# Revit family: APL Metro Series Thermal Heart Hinged Door Open In
name_source: partatom
category: Doors
revit_build: Autodesk Revit LT 2018 (Build: 20170223_1515(x64)
units: mm (PartAtom-declared; Revit-internal decimal feet)

## family parameters
Always vertical = Yes
Cut with Voids When Loaded = No
Host = Wall
OmniClass Number = 23.30.10.00
OmniClass Title = Doors
Room Calculation Point = No
Shared = No

## types (4) — shared parameters
15° Opening = Yes
90° Opening = No
Analytic Construction = <None>
Frame Projection Ext. = 13 mm
Frame Projection Int. = 20 mm  [stored 0.0656168 ft]
Frame Width = 13 mm
Frame Width Sill = 15 mm  [stored 0.0492126 ft]
Function = Interior
Groove = 10 mm  [stored 0.0328084 ft]
Handle = Yes
Handle External = Yes
Handle Internal = Yes
Jamb Liner 1 = Yes
Jamb Liner 2 = Yes
Liner End = 10 mm  [stored 0.0328084 ft]
Liner Head = Yes
Liner Sill = No
Lock External = Yes
Lock Internal = Yes
Opening = Yes
Rough Width = 815 mm  [stored 2.67388 ft]
Wall Closure = By host
Width = 800 mm  [stored 2.62467 ft]
zero-valued in all types: Thickness

## per-type parameters (varying)
| type | Architrave | DG Liner | DG Liner No Groove | Height | Reveal Liner | Rough Height | SG Liner | SG Liner No Groove |
| Architrave (DG) | Yes | No | Yes | 2201 mm | No | 2213 mm | No | No |
| Architrave (SG) | Yes | No | No | 2203 mm | No | 2215 mm  [stored 7.26706 ft] | No | Yes |
| Liner (DG) | No | Yes | No | 2203 mm | Yes | 2215 mm  [stored 7.26706 ft] | No | No |
| Liner (SG) | No | No | No | 2203 mm | Yes | 2215 mm  [stored 7.26706 ft] | Yes | No |

note: [stored X ft] marks values corroborated as IEEE doubles in the binary element streams (Revit-internal decimal feet)

## geometry (parser evidence)
native form markers: Sweep x24
no freeform markers — native parametric forms only
